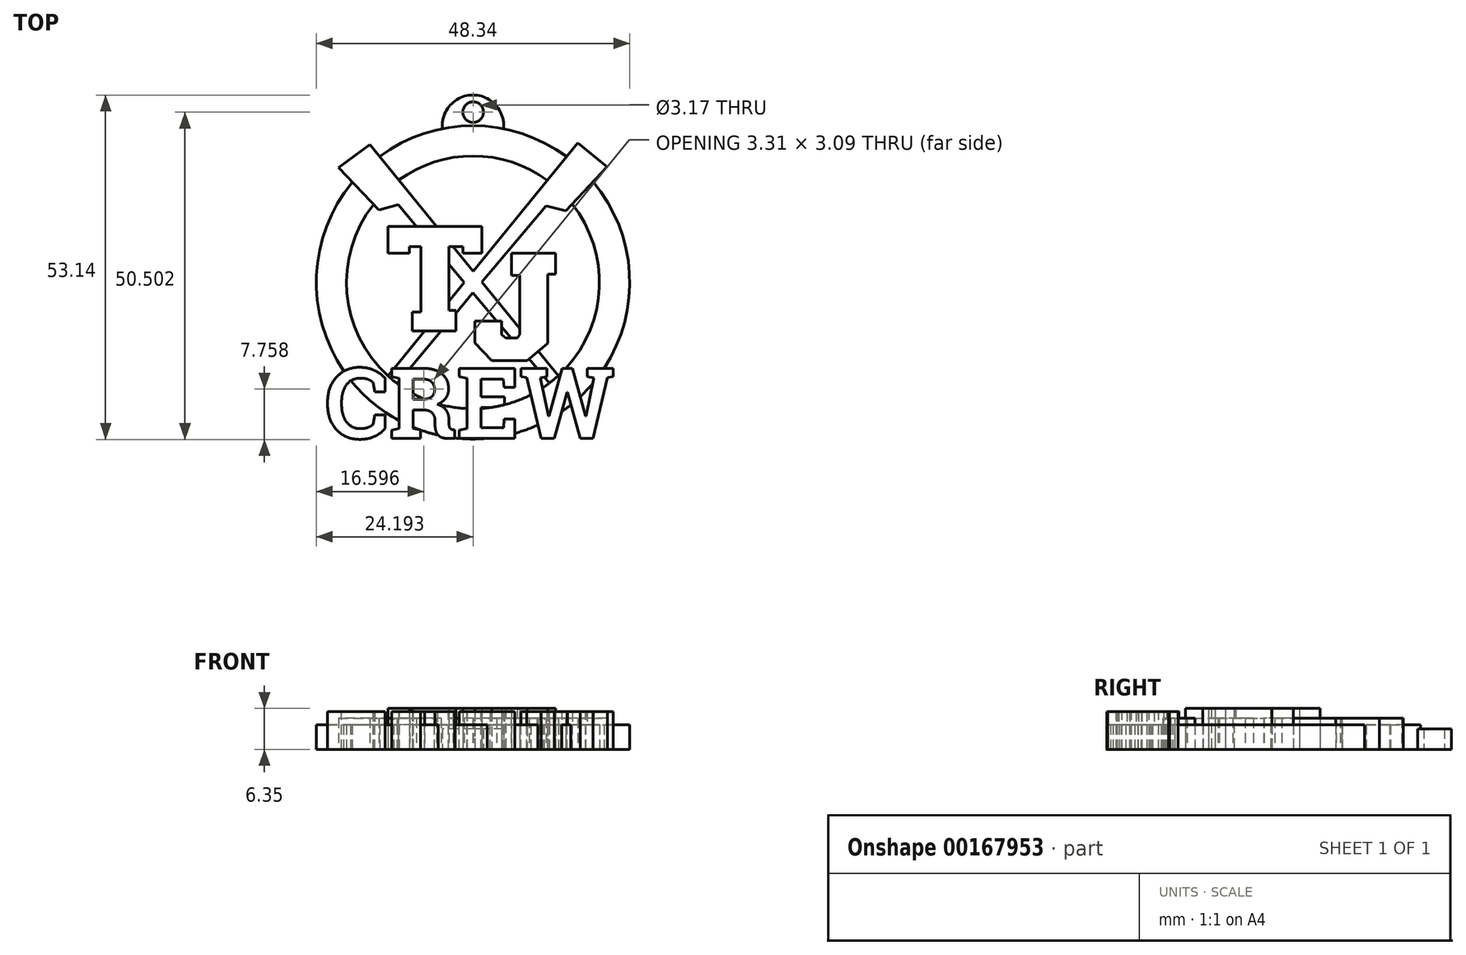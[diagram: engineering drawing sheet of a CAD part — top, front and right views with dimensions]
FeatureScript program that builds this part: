
annotation { "Feature Type Name" : "Feature", "Feature Type Description" : "" }
export const myFeature = defineFeature(function(context is Context, id is Id, definition is map)
    precondition{}
    {
        {
            var Q0;
            Q0=qCreatedBy(makeId("Top.planeOp"),FACE);
            var sketch = newSketch(context, id + "F0", { "sketchPlane" : qUnion([Q0])});
            skLineSegment(sketch, "E0", {"start": v(-21.97, 17.83) * mm, "end": v(-26.79, 14.26) * mm});
            skLineSegment(sketch, "E1", {"start": v(-26.79, 14.26) * mm, "end": v(-20.58, 7.71) * mm});
            skLineSegment(sketch, "E2", {"start": v(-20.58, 7.71) * mm, "end": v(-17.6, 8.59) * mm});
            skLineSegment(sketch, "E3", {"start": v(-17.6, 8.59) * mm, "end": v(-14.75, 5.22) * mm});
            skLineSegment(sketch, "E4", {"start": v(10.03, -24.02) * mm, "end": v(11.3, -22.94) * mm});
            skLineSegment(sketch, "E5", {"start": v(11.3, -22.94) * mm, "end": v(4.04, -14.05) * mm});
            skLineSegment(sketch, "E6", {"start": v(-23.13, -22.7) * mm, "end": v(-13.54, -10.93) * mm});
            skLineSegment(sketch, "E7", {"start": v(10.1, 18.08) * mm, "end": v(14.6, 14.41) * mm});
            skLineSegment(sketch, "E8", {"start": v(14.6, 14.41) * mm, "end": v(8.26, 7.64) * mm});
            skLineSegment(sketch, "E9", {"start": v(8.26, 7.64) * mm, "end": v(5.2, 8.37) * mm});
            skLineSegment(sketch, "E10", {"start": v(5.2, 8.37) * mm, "end": v(-4.66, -3.39) * mm});
            skLineSegment(sketch, "E11", {"start": v(-21.79, -23.8) * mm, "end": v(-23.13, -22.7) * mm});
            skLineSegment(sketch, "E12", {"start": v(-19.13, 5.22) * mm, "end": v(-4.7, 5.22) * mm});
            skLineSegment(sketch, "E13", {"start": v(-4.7, 5.22) * mm, "end": v(-4.7, 1.1) * mm});
            skLineSegment(sketch, "E14", {"start": v(-4.7, 1.1) * mm, "end": v(-7.58, 1.1) * mm});
            skLineSegment(sketch, "E15", {"start": v(-7.58, 1.1) * mm, "end": v(-7.58, 2.09) * mm});
            skLineSegment(sketch, "E16", {"start": v(-7.58, 2.09) * mm, "end": v(-9.79, 2.09) * mm});
            skLineSegment(sketch, "E17", {"start": v(-9.79, 2.09) * mm, "end": v(-9.79, -7.77) * mm});
            skLineSegment(sketch, "E18", {"start": v(-9.79, -7.77) * mm, "end": v(-8.69, -7.77) * mm});
            skLineSegment(sketch, "E19", {"start": v(-8.69, -7.77) * mm, "end": v(-8.69, -10.93) * mm});
            skLineSegment(sketch, "E20", {"start": v(-8.69, -10.93) * mm, "end": v(-15.43, -10.93) * mm});
            skLineSegment(sketch, "E21", {"start": v(-15.43, -10.93) * mm, "end": v(-15.43, -8.02) * mm});
            skLineSegment(sketch, "E22", {"start": v(-15.43, -8.02) * mm, "end": v(-14.1, -8.02) * mm});
            skLineSegment(sketch, "E23", {"start": v(-14.1, -8.02) * mm, "end": v(-14.1, 2.09) * mm});
            skLineSegment(sketch, "E24", {"start": v(-14.1, 2.09) * mm, "end": v(-15.88, 2.09) * mm});
            skLineSegment(sketch, "E25", {"start": v(-15.88, 2.09) * mm, "end": v(-15.88, 1.1) * mm});
            skLineSegment(sketch, "E26", {"start": v(-15.88, 1.1) * mm, "end": v(-19.13, 1.1) * mm});
            skLineSegment(sketch, "E27", {"start": v(-19.13, 1.1) * mm, "end": v(-19.13, 5.22) * mm});
            skLineSegment(sketch, "E28", {"start": v(-0.09, 1.1) * mm, "end": v(6.71, 1.1) * mm});
            skLineSegment(sketch, "E29", {"start": v(6.71, 1.1) * mm, "end": v(6.71, -2.18) * mm});
            skLineSegment(sketch, "E30", {"start": v(6.71, -2.18) * mm, "end": v(5.46, -2.18) * mm});
            skLineSegment(sketch, "E31", {"start": v(5.46, -2.18) * mm, "end": v(5.46, -12.84) * mm});
            skLineSegment(sketch, "E32", {"start": v(5.46, -12.84) * mm, "end": v(2.31, -15.51) * mm});
            skLineSegment(sketch, "E33", {"start": v(2.31, -15.51) * mm, "end": v(-3.16, -15.51) * mm});
            skLineSegment(sketch, "E34", {"start": v(-3.16, -15.51) * mm, "end": v(-5.75, -12.79) * mm});
            skLineSegment(sketch, "E35", {"start": v(-5.75, -12.79) * mm, "end": v(-5.75, -9.39) * mm});
            skLineSegment(sketch, "E36", {"start": v(-5.75, -9.39) * mm, "end": v(-1.61, -9.39) * mm});
            skLineSegment(sketch, "E37", {"start": v(-1.61, -9.39) * mm, "end": v(-1.61, -11.48) * mm});
            skLineSegment(sketch, "E38", {"start": v(-1.61, -11.48) * mm, "end": v(-1, -11.98) * mm});
            skLineSegment(sketch, "E39", {"start": v(-1, -11.98) * mm, "end": v(0.76, -11.98) * mm});
            skLineSegment(sketch, "E40", {"start": v(0.76, -11.98) * mm, "end": v(1.17, -11.48) * mm});
            skLineSegment(sketch, "E41", {"start": v(1.17, -11.48) * mm, "end": v(1.17, -2.34) * mm});
            skLineSegment(sketch, "E42", {"start": v(1.17, -2.34) * mm, "end": v(-0.09, -2.34) * mm});
            skLineSegment(sketch, "E43", {"start": v(-0.09, -2.34) * mm, "end": v(-0.09, 1.1) * mm});
            skLineSegment(sketch, "E44.trimOffspring", {"start": v(-11.68, 5.22) * mm, "end": v(-21.97, 17.83) * mm});
            skLineSegment(sketch, "E45.trimOffspring", {"start": v(-9.79, -0.63) * mm, "end": v(-7.42, -3.42) * mm});
            skLineSegment(sketch, "E46.trimOffspring", {"start": v(-6.03, -1.7) * mm, "end": v(-9.12, 2.09) * mm});
            skLineSegment(sketch, "E47.trimOffspring", {"start": v(-6.05, -5.05) * mm, "end": v(-2.37, -9.39) * mm});
            skLineSegment(sketch, "E48.trimOffspring", {"start": v(-6.05, -5.05) * mm, "end": v(-8.69, -8.2) * mm});
            skLineSegment(sketch, "E49.trimOffspring", {"start": v(-6.03, -1.7) * mm, "end": v(10.1, 18.08) * mm});
            skLineSegment(sketch, "E50.trimOffspring", {"start": v(-1.61, -10.28) * mm, "end": v(-0.17, -11.98) * mm});
            skLineSegment(sketch, "E51.trimOffspring", {"start": v(1.17, -10.53) * mm, "end": v(-4.66, -3.39) * mm});
            skLineSegment(sketch, "E52.trimOffspring", {"start": v(2.6, -15.26) * mm, "end": v(10.03, -24.02) * mm});
            skLineSegment(sketch, "E53.trimOffspring", {"start": v(-9.79, -6.33) * mm, "end": v(-7.42, -3.42) * mm});
            skLineSegment(sketch, "E54.trimOffspring", {"start": v(-10.98, -10.93) * mm, "end": v(-21.79, -23.8) * mm});
            skText(sketch, "E55", { "text": "CREW", "fontName": "RobotoSlab-Bold.ttf"});
            skCircle(sketch, "E56", {"center": v(-6.05, -3.42) * mm, "radius": 24.17 * mm});
            skCircle(sketch, "E57", {"center": v(-6.05, -3.42) * mm, "radius": 19.5 * mm});
            skArc(sketch, "E58", {"start": v(-6.74, 16.06) * mm, "mid": v(-6.05, 16.01) * mm, "end": v(-5.36, 16.06) * mm});
            skCircle(sketch, "E59", {"center": v(-6.03, 22.84) * mm, "radius": 1.59 * mm});
            skArc(sketch, "E60.trimOffspring", {"start": v(-1.34, 20.29) * mm, "mid": v(-6.05, 25.48) * mm, "end": v(-10.76, 20.29) * mm});
            const initialGuessF0  = {"E55": [-0.02883, -0.0276, 1, 0, 0.01097]};
            skSetInitialGuess(sketch, initialGuessF0);
            skSolve(sketch);
        }
        {
            var Q0;
            {var subQ0=sQuery(id+"F0.wireOp",EDGE,"E55.sketch_text.stroke-101");Q0=makeQuery(id+"F0.imprint","IMPRINT",FACE,{"disambiguationData":[TD([[makeQuery(id+"F0.imprint","IMPRINT",EDGE,{"derivedFrom":subQ0}),1.0]])]});}
            var Q1;
            {var subQ1=sQuery(id+"F0.wireOp",EDGE,"E56");var subQ10=sQuery(id+"F0.wireOp",EDGE,"E44.trimOffspring");var subQ12=makeQuery(id+"F0.imprint","INTERSECT",VERTEX,{"derivedFrom":[subQ10,subQ1]});Q1=makeQuery(id+"F0.imprint","IMPRINT",FACE,{"disambiguationData":[TD([[makeQuery(id+"F0.imprint","IMPRINT",EDGE,{"disambiguationData":[TD([[subQ12,1.0]])],"derivedFrom":subQ10}),-1.0]])]});}
            var Q2;
            {var subQ0=sQuery(id+"F0.wireOp",EDGE,"E55.sketch_text.stroke-21");Q2=makeQuery(id+"F0.imprint","IMPRINT",FACE,{"disambiguationData":[TD([[makeQuery(id+"F0.imprint","IMPRINT",EDGE,{"derivedFrom":subQ0}),1.0]])]});}
            var Q3;
            {var subQ0=sQuery(id+"F0.wireOp",EDGE,"E56");var subQ1=sQuery(id+"F0.wireOp",EDGE,"E54.trimOffspring");var subQ2=makeQuery(id+"F0.imprint","INTERSECT",VERTEX,{"derivedFrom":[subQ1,subQ0]});Q3=makeQuery(id+"F0.imprint","IMPRINT",FACE,{"disambiguationData":[TD([[makeQuery(id+"F0.imprint","IMPRINT",EDGE,{"disambiguationData":[TD([[subQ2,1.0]])],"derivedFrom":subQ1}),1.0]])]});}
            var Q4;
            {var subQ1=sQuery(id+"F0.wireOp",EDGE,"E55.sketch_text.stroke-2");Q4=makeQuery(id+"F0.imprint","IMPRINT",FACE,{"disambiguationData":[TD([[makeQuery(id+"F0.imprint","IMPRINT",EDGE,{"derivedFrom":subQ1}),1.0]])]});}
            var Q5;
            {var subQ0=sQuery(id+"F0.wireOp",EDGE,"E55.sketch_text.stroke-38");Q5=makeQuery(id+"F0.imprint","IMPRINT",FACE,{"disambiguationData":[TD([[makeQuery(id+"F0.imprint","IMPRINT",EDGE,{"derivedFrom":subQ0}),1.0]])]});}
            var Q6;
            {var subQ4=sQuery(id+"F0.wireOp",EDGE,"E55.sketch_text.stroke-28");Q6=makeQuery(id+"F0.imprint","IMPRINT",FACE,{"disambiguationData":[TD([[makeQuery(id+"F0.imprint","IMPRINT",EDGE,{"derivedFrom":subQ4}),1.0]])]});}
            var Q7;
            {var subQ0=sQuery(id+"F0.wireOp",EDGE,"E55.sketch_text.stroke-53");Q7=makeQuery(id+"F0.imprint","IMPRINT",FACE,{"disambiguationData":[TD([[makeQuery(id+"F0.imprint","IMPRINT",EDGE,{"derivedFrom":subQ0}),1.0]])]});}
            var Q8;
            {var subQ15=sQuery(id+"F0.wireOp",EDGE,"E55.sketch_text.stroke-62");Q8=makeQuery(id+"F0.imprint","IMPRINT",FACE,{"disambiguationData":[TD([[makeQuery(id+"F0.imprint","IMPRINT",EDGE,{"derivedFrom":subQ15}),1.0]])]});}
            var Q9;
            {var subQ0=sQuery(id+"F0.wireOp",EDGE,"E55.sketch_text.stroke-95");Q9=makeQuery(id+"F0.imprint","IMPRINT",FACE,{"disambiguationData":[TD([[makeQuery(id+"F0.imprint","IMPRINT",EDGE,{"derivedFrom":subQ0}),1.0]])]});}
            var Q10;
            {var subQ0=sQuery(id+"F0.wireOp",EDGE,"E55.sketch_text.stroke-96");var subQ1=sQuery(id+"F0.wireOp",EDGE,"E5");var subQ2=makeQuery(id+"F0.imprint","INTERSECT",VERTEX,{"derivedFrom":[subQ1,subQ0]});Q10=makeQuery(id+"F0.imprint","IMPRINT",FACE,{"disambiguationData":[TD([[makeQuery(id+"F0.imprint","IMPRINT",EDGE,{"disambiguationData":[TD([[subQ2,-1.0]])],"derivedFrom":subQ1}),-1.0]])]});}
            var Q11;
            {var subQ0=sQuery(id+"F0.wireOp",EDGE,"E56");var subQ1=sQuery(id+"F0.wireOp",EDGE,"E52.trimOffspring");var subQ2=makeQuery(id+"F0.imprint","INTERSECT",VERTEX,{"derivedFrom":[subQ1,subQ0]});Q11=makeQuery(id+"F0.imprint","IMPRINT",FACE,{"disambiguationData":[TD([[makeQuery(id+"F0.imprint","IMPRINT",EDGE,{"disambiguationData":[TD([[subQ2,1.0]])],"derivedFrom":subQ1}),-1.0]])]});}
            var Q12;
            {var subQ1=sQuery(id+"F0.wireOp",EDGE,"E55.sketch_text.stroke-85");Q12=makeQuery(id+"F0.imprint","IMPRINT",FACE,{"disambiguationData":[TD([[makeQuery(id+"F0.imprint","IMPRINT",EDGE,{"derivedFrom":subQ1}),1.0]])]});}
            var Q13;
            {var subQ5=sQuery(id+"F0.wireOp",EDGE,"E55.sketch_text.stroke-0");Q13=makeQuery(id+"F0.imprint","IMPRINT",FACE,{"disambiguationData":[TD([[makeQuery(id+"F0.imprint","IMPRINT",EDGE,{"derivedFrom":subQ5}),1.0]])]});}
            var Q14;
            {var subQ0=sQuery(id+"F0.wireOp",EDGE,"E55.sketch_text.stroke-96");var subQ1=sQuery(id+"F0.wireOp",EDGE,"E5");var subQ2=makeQuery(id+"F0.imprint","INTERSECT",VERTEX,{"derivedFrom":[subQ1,subQ0]});Q14=makeQuery(id+"F0.imprint","IMPRINT",FACE,{"disambiguationData":[TD([[makeQuery(id+"F0.imprint","IMPRINT",EDGE,{"disambiguationData":[TD([[subQ2,-1.0]])],"derivedFrom":subQ1}),1.0]])]});}
            var Q15;
            {var subQ1=sQuery(id+"F0.wireOp",EDGE,"E55.sketch_text.stroke-2");Q15=makeQuery(id+"F0.imprint","IMPRINT",FACE,{"disambiguationData":[TD([[makeQuery(id+"F0.imprint","IMPRINT",EDGE,{"derivedFrom":subQ1}),-1.0]])]});}
            var Q16;
            {var subQ5=sQuery(id+"F0.wireOp",EDGE,"E55.sketch_text.stroke-0");Q16=makeQuery(id+"F0.imprint","IMPRINT",FACE,{"disambiguationData":[TD([[makeQuery(id+"F0.imprint","IMPRINT",EDGE,{"derivedFrom":subQ5}),-1.0]])]});}
            var Q17;
            {var subQ4=sQuery(id+"F0.wireOp",EDGE,"E55.sketch_text.stroke-28");Q17=makeQuery(id+"F0.imprint","IMPRINT",FACE,{"disambiguationData":[TD([[makeQuery(id+"F0.imprint","IMPRINT",EDGE,{"derivedFrom":subQ4}),-1.0]])]});}
            var Q18;
            {var subQ2=sQuery(id+"F0.wireOp",EDGE,"E55.sketch_text.stroke-62");Q18=makeQuery(id+"F0.imprint","IMPRINT",FACE,{"disambiguationData":[TD([[makeQuery(id+"F0.imprint","IMPRINT",EDGE,{"derivedFrom":subQ2}),-1.0]])]});}
            var Q19;
            {var subQ0=sQuery(id+"F0.wireOp",EDGE,"E55.sketch_text.stroke-95");Q19=makeQuery(id+"F0.imprint","IMPRINT",FACE,{"disambiguationData":[TD([[makeQuery(id+"F0.imprint","IMPRINT",EDGE,{"derivedFrom":subQ0}),-1.0]])]});}
            var Q20;
            {var subQ6=sQuery(id+"F0.wireOp",EDGE,"E5");var subQ9=sQuery(id+"F0.wireOp",EDGE,"E56");var subQ11=makeQuery(id+"F0.imprint","INTERSECT",VERTEX,{"derivedFrom":[subQ6,subQ9]});Q20=makeQuery(id+"F0.imprint","IMPRINT",FACE,{"disambiguationData":[TD([[makeQuery(id+"F0.imprint","IMPRINT",EDGE,{"disambiguationData":[TD([[subQ11,-1.0]])],"derivedFrom":subQ6}),-1.0]])]});}
            var Q21;
            {var subQ0=sQuery(id+"F0.wireOp",EDGE,"E55.sketch_text.stroke-85");Q21=makeQuery(id+"F0.imprint","IMPRINT",FACE,{"disambiguationData":[TD([[makeQuery(id+"F0.imprint","IMPRINT",EDGE,{"derivedFrom":subQ0}),-1.0]])]});}
            var Q22;
            {var subQ4=sQuery(id+"F0.wireOp",EDGE,"E55.sketch_text.stroke-101");Q22=makeQuery(id+"F0.imprint","IMPRINT",FACE,{"disambiguationData":[TD([[makeQuery(id+"F0.imprint","IMPRINT",EDGE,{"derivedFrom":subQ4}),-1.0]])]});}
            var Q23;
            {var subQ0=sQuery(id+"F0.wireOp",EDGE,"E55.sketch_text.stroke-80");var subQ1=sQuery(id+"F0.wireOp",EDGE,"E55.sketch_text.stroke-60");var subQ2=makeQuery(id+"F0.imprint","INTERSECT",VERTEX,{"derivedFrom":[subQ1,subQ0]});Q23=makeQuery(id+"F0.imprint","IMPRINT",FACE,{"disambiguationData":[TD([[makeQuery(id+"F0.imprint","IMPRINT",EDGE,{"disambiguationData":[TD([[subQ2,-1.0]])],"derivedFrom":subQ1}),-1.0]])]});}
            extrude(context, id + "F1", {"entities" : qUnion([Q0, Q1, Q2, Q3, Q4, Q5, Q6, Q7, Q8, Q9, Q10, Q11, Q12, Q13, Q14, Q15, Q16, Q17, Q18, Q19, Q20, Q21, Q22, Q23]), "depth" : 3.8 * mm});
        }
        {
            var Q0;
            {var subQ4=sQuery(id+"F0.wireOp",EDGE,"E2");Q0=makeQuery(id+"F0.imprint","IMPRINT",FACE,{"disambiguationData":[TD([[makeQuery(id+"F0.imprint","IMPRINT",EDGE,{"derivedFrom":subQ4}),1.0]])]});}
            var Q1;
            {var subQ0=sQuery(id+"F0.wireOp",EDGE,"E56");var subQ1=sQuery(id+"F0.wireOp",EDGE,"E1");var subQ2=makeQuery(id+"F0.imprint","INTERSECT",VERTEX,{"derivedFrom":[subQ1,subQ0]});Q1=makeQuery(id+"F0.imprint","IMPRINT",FACE,{"disambiguationData":[TD([[makeQuery(id+"F0.imprint","IMPRINT",EDGE,{"disambiguationData":[TD([[subQ2,-1.0]])],"derivedFrom":subQ1}),1.0]])]});}
            var Q2;
            {var subQ0=sQuery(id+"F0.wireOp",EDGE,"E0");Q2=makeQuery(id+"F0.imprint","IMPRINT",FACE,{"disambiguationData":[TD([[makeQuery(id+"F0.imprint","IMPRINT",EDGE,{"derivedFrom":subQ0}),1.0]])]});}
            var Q3;
            {var subQ0=sQuery(id+"F0.wireOp",EDGE,"E56");var subQ1=sQuery(id+"F0.wireOp",EDGE,"E8");var subQ2=makeQuery(id+"F0.imprint","INTERSECT",VERTEX,{"derivedFrom":[subQ1,subQ0]});Q3=makeQuery(id+"F0.imprint","IMPRINT",FACE,{"disambiguationData":[TD([[makeQuery(id+"F0.imprint","IMPRINT",EDGE,{"disambiguationData":[TD([[subQ2,-1.0]])],"derivedFrom":subQ1}),-1.0]])]});}
            var Q4;
            {var subQ0=sQuery(id+"F0.wireOp",EDGE,"E7");Q4=makeQuery(id+"F0.imprint","IMPRINT",FACE,{"disambiguationData":[TD([[makeQuery(id+"F0.imprint","IMPRINT",EDGE,{"derivedFrom":subQ0}),-1.0]])]});}
            var Q5;
            {var subQ7=sQuery(id+"F0.wireOp",EDGE,"E9");Q5=makeQuery(id+"F0.imprint","IMPRINT",FACE,{"disambiguationData":[TD([[makeQuery(id+"F0.imprint","IMPRINT",EDGE,{"derivedFrom":subQ7}),-1.0]])]});}
            var Q6;
            {var subQ1=sQuery(id+"F0.wireOp",EDGE,"E20");var subQ5=sQuery(id+"F0.wireOp",EDGE,"E6");var subQ6=makeQuery(id+"F0.imprint","INTERSECT",VERTEX,{"derivedFrom":[subQ5,subQ1]});Q6=makeQuery(id+"F0.imprint","IMPRINT",FACE,{"disambiguationData":[TD([[makeQuery(id+"F0.imprint","IMPRINT",EDGE,{"disambiguationData":[TD([[subQ6,1.0]])],"derivedFrom":subQ5}),-1.0]])]});}
            var Q7;
            {var subQ12=sQuery(id+"F0.wireOp",EDGE,"E55.sketch_text.stroke-92");Q7=makeQuery(id+"F0.imprint","IMPRINT",FACE,{"disambiguationData":[TD([[makeQuery(id+"F0.imprint","IMPRINT",EDGE,{"derivedFrom":subQ12}),1.0]])]});}
            var Q8;
            {var subQ0=sQuery(id+"F0.wireOp",EDGE,"E55.sketch_text.stroke-49");Q8=makeQuery(id+"F0.imprint","IMPRINT",FACE,{"disambiguationData":[TD([[makeQuery(id+"F0.imprint","IMPRINT",EDGE,{"derivedFrom":subQ0}),1.0]])]});}
            var Q9;
            {var subQ0=sQuery(id+"F0.wireOp",EDGE,"E55.sketch_text.stroke-49");Q9=makeQuery(id+"F0.imprint","IMPRINT",FACE,{"disambiguationData":[TD([[makeQuery(id+"F0.imprint","IMPRINT",EDGE,{"derivedFrom":subQ0}),-1.0]])]});}
            var Q10;
            {var subQ5=sQuery(id+"F0.wireOp",EDGE,"E55.sketch_text.stroke-92");Q10=makeQuery(id+"F0.imprint","IMPRINT",FACE,{"disambiguationData":[TD([[makeQuery(id+"F0.imprint","IMPRINT",EDGE,{"derivedFrom":subQ5}),-1.0]])]});}
            extrude(context, id + "F2", {"entities" : qUnion([Q0, Q1, Q2, Q3, Q4, Q5, Q6, Q7, Q8, Q9, Q10]), "operationType" : NewBodyOperationType.ADD, "depth" : 4.83 * mm});
        }
        {
            var Q0;
            {var subQ17=sQuery(id+"F0.wireOp",EDGE,"E13");Q0=makeQuery(id+"F0.imprint","IMPRINT",FACE,{"disambiguationData":[TD([[makeQuery(id+"F0.imprint","IMPRINT",EDGE,{"derivedFrom":subQ17}),-1.0]])]});}
            var Q1;
            Q1=makeQuery(id+"F0.imprint","IMPRINT",FACE,{"disambiguationData":[TD([[makeQuery(id+"F0.imprint","IMPRINT",EDGE,{"derivedFrom":sQuery(id+"F0.wireOp",EDGE,"E28")}),-1.0]])]});
            extrude(context, id + "F3", {"entities" : qUnion([Q0, Q1]), "operationType" : NewBodyOperationType.ADD, "depth" : 6.35 * mm});
        }
        {
            var Q0;
            Q0=makeQuery(id+"F0.imprint","IMPRINT",FACE,{"disambiguationData":[TD([[makeQuery(id+"F0.imprint","IMPRINT",EDGE,{"derivedFrom":sQuery(id+"F0.wireOp",EDGE,"E59")}),-1.0]])]});
            extrude(context, id + "F4", {"entities" : qUnion([Q0]), "operationType" : NewBodyOperationType.ADD, "depth" : 3.17 * mm});
        }
        {
            var Q0;
            Q0=makeQuery(id+"F1.opExtrude","CAP_FACE",FACE,{"disambiguationData":[OSD([sQuery(id+"F0.wireOp",EDGE,"E1"),sQuery(id+"F0.wireOp",EDGE,"E8"),sQuery(id+"F0.wireOp",EDGE,"E56"),sQuery(id+"F0.wireOp",EDGE,"E57")])],"isStart":false});
            var sketch = newSketch(context, id + "F5", { "sketchPlane" : qUnion([Q0])});
            skText(sketch, "E61", { "text": "CREW", "fontName": "RobotoSlab-Bold.ttf"});
            const initialGuessF5  = {"E61": [-0.02887, -0.0275, 1, 0, 0.01095]};
            skSetInitialGuess(sketch, initialGuessF5);
            skSolve(sketch);
        }
        {
            var Q0;
            {var subQ0=sQuery(id+"F5.wireOp",EDGE,"E61.sketch_text.stroke-5");Q0=makeQuery(id+"F5.imprint","IMPRINT",FACE,{"disambiguationData":[TD([[makeQuery(id+"F5.imprint","IMPRINT",EDGE,{"derivedFrom":subQ0}),-1.0]])]});}
            var Q1;
            Q1=makeQuery(id+"F5.imprint","IMPRINT",FACE,{"disambiguationData":[TD([[makeQuery(id+"F5.imprint","IMPRINT",EDGE,{"derivedFrom":sQuery(id+"F5.wireOp",EDGE,"E61.sketch_text.stroke-0")}),-1.0]])]});
            var Q2;
            Q2=makeQuery(id+"F5.imprint","IMPRINT",FACE,{"disambiguationData":[TD([[makeQuery(id+"F5.imprint","IMPRINT",EDGE,{"derivedFrom":sQuery(id+"F5.wireOp",EDGE,"E61.sketch_text.stroke-24")}),-1.0]])]});
            var Q3;
            {var subQ75=sQuery(id+"F5.wireOp",EDGE,"E61.sketch_text.stroke-28");Q3=makeQuery(id+"F5.imprint","IMPRINT",FACE,{"disambiguationData":[TD([[makeQuery(id+"F5.imprint","IMPRINT",EDGE,{"derivedFrom":subQ75}),-1.0]])]});}
            var Q4;
            {var subQ0=sQuery(id+"F5.wireOp",EDGE,"E61.sketch_text.stroke-45");Q4=makeQuery(id+"F5.imprint","IMPRINT",FACE,{"disambiguationData":[TD([[makeQuery(id+"F5.imprint","IMPRINT",EDGE,{"derivedFrom":subQ0}),-1.0]])]});}
            var Q5;
            {var subQ72=sQuery(id+"F5.wireOp",EDGE,"E61.sketch_text.stroke-62");Q5=makeQuery(id+"F5.imprint","IMPRINT",FACE,{"disambiguationData":[TD([[makeQuery(id+"F5.imprint","IMPRINT",EDGE,{"derivedFrom":subQ72}),-1.0]])]});}
            var Q6;
            {var subQ0=sQuery(id+"F5.wireOp",EDGE,"E61.sketch_text.stroke-66");var subQ1=sQuery(id+"F5.wireOp",EDGE,"E61.sketch_text.stroke-65");var subQ2=makeQuery(id+"F5.imprint","INTERSECT",VERTEX,{"derivedFrom":[subQ1,subQ0]});Q6=makeQuery(id+"F5.imprint","IMPRINT",FACE,{"disambiguationData":[TD([[makeQuery(id+"F5.imprint","IMPRINT",EDGE,{"disambiguationData":[TD([[subQ2,1.0]])],"derivedFrom":subQ1}),-1.0]])]});}
            var Q7;
            {var subQ44=sQuery(id+"F5.wireOp",EDGE,"E61.sketch_text.stroke-70");Q7=makeQuery(id+"F5.imprint","IMPRINT",FACE,{"disambiguationData":[TD([[makeQuery(id+"F5.imprint","IMPRINT",EDGE,{"derivedFrom":subQ44}),-1.0]])]});}
            var Q8;
            {var subQ0=sQuery(id+"F5.wireOp",EDGE,"E61.sketch_text.stroke-89");Q8=makeQuery(id+"F5.imprint","IMPRINT",FACE,{"disambiguationData":[TD([[makeQuery(id+"F5.imprint","IMPRINT",EDGE,{"derivedFrom":subQ0}),-1.0]])]});}
            var Q9;
            {var subQ78=sQuery(id+"F5.wireOp",EDGE,"E61.sketch_text.stroke-85");Q9=makeQuery(id+"F5.imprint","IMPRINT",FACE,{"disambiguationData":[TD([[makeQuery(id+"F5.imprint","IMPRINT",EDGE,{"derivedFrom":subQ78}),-1.0]])]});}
            var Q10;
            {var subQ0=sQuery(id+"F5.wireOp",EDGE,"E61.sketch_text.stroke-87");Q10=makeQuery(id+"F5.imprint","IMPRINT",FACE,{"disambiguationData":[TD([[makeQuery(id+"F5.imprint","IMPRINT",EDGE,{"derivedFrom":subQ0}),-1.0]])]});}
            var Q11;
            {var subQ0=sQuery(id+"F5.wireOp",EDGE,"E61.sketch_text.stroke-97");var subQ1=sQuery(id+"F5.wireOp",EDGE,"E61.sketch_text.stroke-96");var subQ2=makeQuery(id+"F5.imprint","INTERSECT",VERTEX,{"derivedFrom":[subQ1,subQ0]});Q11=makeQuery(id+"F5.imprint","IMPRINT",FACE,{"disambiguationData":[TD([[makeQuery(id+"F5.imprint","IMPRINT",EDGE,{"disambiguationData":[TD([[subQ2,1.0]])],"derivedFrom":subQ1}),-1.0]])]});}
            var Q12;
            Q12=makeQuery(id+"F5.imprint","IMPRINT",FACE,{"disambiguationData":[TD([[makeQuery(id+"F5.imprint","IMPRINT",EDGE,{"derivedFrom":sQuery(id+"F5.wireOp",EDGE,"E61.sketch_text.stroke-81")}),-1.0]])]});
            var Q13;
            {var subQ23=sQuery(id+"F5.wireOp",EDGE,"E61.sketch_text.stroke-101");Q13=makeQuery(id+"F5.imprint","IMPRINT",FACE,{"disambiguationData":[TD([[makeQuery(id+"F5.imprint","IMPRINT",EDGE,{"derivedFrom":subQ23}),-1.0]])]});}
            var Q14;
            {var subQ0=sQuery(id+"F5.wireOp",EDGE,"E61.sketch_text.stroke-35");Q14=makeQuery(id+"F5.imprint","IMPRINT",FACE,{"disambiguationData":[TD([[makeQuery(id+"F5.imprint","IMPRINT",EDGE,{"derivedFrom":subQ0}),-1.0]])]});}
            extrude(context, id + "F6", {"entities" : qUnion([Q0, Q1, Q2, Q3, Q4, Q5, Q6, Q7, Q8, Q9, Q10, Q11, Q12, Q13, Q14]), "operationType" : NewBodyOperationType.ADD, "oppositeDirection" : true, "depth" : 3.8 * mm});
        }
        {
            var Q0;
            Q0=makeQuery(id+"F5.imprint","IMPRINT",FACE,{"disambiguationData":[TD([[makeQuery(id+"F5.imprint","IMPRINT",EDGE,{"derivedFrom":sQuery(id+"F5.wireOp",EDGE,"E61.sketch_text.stroke-0")}),-1.0]])]});
            var Q1;
            {var subQ75=sQuery(id+"F5.wireOp",EDGE,"E61.sketch_text.stroke-28");Q1=makeQuery(id+"F5.imprint","IMPRINT",FACE,{"disambiguationData":[TD([[makeQuery(id+"F5.imprint","IMPRINT",EDGE,{"derivedFrom":subQ75}),-1.0]])]});}
            var Q2;
            {var subQ0=sQuery(id+"F5.wireOp",EDGE,"E61.sketch_text.stroke-45");Q2=makeQuery(id+"F5.imprint","IMPRINT",FACE,{"disambiguationData":[TD([[makeQuery(id+"F5.imprint","IMPRINT",EDGE,{"derivedFrom":subQ0}),-1.0]])]});}
            var Q3;
            {var subQ72=sQuery(id+"F5.wireOp",EDGE,"E61.sketch_text.stroke-62");Q3=makeQuery(id+"F5.imprint","IMPRINT",FACE,{"disambiguationData":[TD([[makeQuery(id+"F5.imprint","IMPRINT",EDGE,{"derivedFrom":subQ72}),-1.0]])]});}
            var Q4;
            {var subQ44=sQuery(id+"F5.wireOp",EDGE,"E61.sketch_text.stroke-70");Q4=makeQuery(id+"F5.imprint","IMPRINT",FACE,{"disambiguationData":[TD([[makeQuery(id+"F5.imprint","IMPRINT",EDGE,{"derivedFrom":subQ44}),-1.0]])]});}
            var Q5;
            {var subQ0=sQuery(id+"F5.wireOp",EDGE,"E61.sketch_text.stroke-66");var subQ1=sQuery(id+"F5.wireOp",EDGE,"E61.sketch_text.stroke-65");var subQ2=makeQuery(id+"F5.imprint","INTERSECT",VERTEX,{"derivedFrom":[subQ1,subQ0]});Q5=makeQuery(id+"F5.imprint","IMPRINT",FACE,{"disambiguationData":[TD([[makeQuery(id+"F5.imprint","IMPRINT",EDGE,{"disambiguationData":[TD([[subQ2,1.0]])],"derivedFrom":subQ1}),-1.0]])]});}
            var Q6;
            {var subQ0=sQuery(id+"F5.wireOp",EDGE,"E61.sketch_text.stroke-89");Q6=makeQuery(id+"F5.imprint","IMPRINT",FACE,{"disambiguationData":[TD([[makeQuery(id+"F5.imprint","IMPRINT",EDGE,{"derivedFrom":subQ0}),-1.0]])]});}
            var Q7;
            {var subQ78=sQuery(id+"F5.wireOp",EDGE,"E61.sketch_text.stroke-85");Q7=makeQuery(id+"F5.imprint","IMPRINT",FACE,{"disambiguationData":[TD([[makeQuery(id+"F5.imprint","IMPRINT",EDGE,{"derivedFrom":subQ78}),-1.0]])]});}
            var Q8;
            {var subQ0=sQuery(id+"F5.wireOp",EDGE,"E61.sketch_text.stroke-87");Q8=makeQuery(id+"F5.imprint","IMPRINT",FACE,{"disambiguationData":[TD([[makeQuery(id+"F5.imprint","IMPRINT",EDGE,{"derivedFrom":subQ0}),-1.0]])]});}
            var Q9;
            Q9=makeQuery(id+"F5.imprint","IMPRINT",FACE,{"disambiguationData":[TD([[makeQuery(id+"F5.imprint","IMPRINT",EDGE,{"derivedFrom":sQuery(id+"F5.wireOp",EDGE,"E61.sketch_text.stroke-81")}),-1.0]])]});
            var Q10;
            {var subQ0=sQuery(id+"F5.wireOp",EDGE,"E61.sketch_text.stroke-97");var subQ1=sQuery(id+"F5.wireOp",EDGE,"E61.sketch_text.stroke-96");var subQ2=makeQuery(id+"F5.imprint","INTERSECT",VERTEX,{"derivedFrom":[subQ1,subQ0]});Q10=makeQuery(id+"F5.imprint","IMPRINT",FACE,{"disambiguationData":[TD([[makeQuery(id+"F5.imprint","IMPRINT",EDGE,{"disambiguationData":[TD([[subQ2,1.0]])],"derivedFrom":subQ1}),-1.0]])]});}
            var Q11;
            {var subQ23=sQuery(id+"F5.wireOp",EDGE,"E61.sketch_text.stroke-101");Q11=makeQuery(id+"F5.imprint","IMPRINT",FACE,{"disambiguationData":[TD([[makeQuery(id+"F5.imprint","IMPRINT",EDGE,{"derivedFrom":subQ23}),-1.0]])]});}
            var Q12;
            {var subQ0=sQuery(id+"F5.wireOp",EDGE,"E61.sketch_text.stroke-5");Q12=makeQuery(id+"F5.imprint","IMPRINT",FACE,{"disambiguationData":[TD([[makeQuery(id+"F5.imprint","IMPRINT",EDGE,{"derivedFrom":subQ0}),-1.0]])]});}
            var Q13;
            {var subQ0=sQuery(id+"F5.wireOp",EDGE,"E61.sketch_text.stroke-35");Q13=makeQuery(id+"F5.imprint","IMPRINT",FACE,{"disambiguationData":[TD([[makeQuery(id+"F5.imprint","IMPRINT",EDGE,{"derivedFrom":subQ0}),-1.0]])]});}
            var Q14;
            Q14=makeQuery(id+"F5.imprint","IMPRINT",FACE,{"disambiguationData":[TD([[makeQuery(id+"F5.imprint","IMPRINT",EDGE,{"derivedFrom":sQuery(id+"F5.wireOp",EDGE,"E61.sketch_text.stroke-24")}),-1.0]])]});
            extrude(context, id + "F7", {"entities" : qUnion([Q0, Q1, Q2, Q3, Q4, Q5, Q6, Q7, Q8, Q9, Q10, Q11, Q12, Q13, Q14]), "operationType" : NewBodyOperationType.ADD, "depth" : 2.03 * mm});
        }
    });
